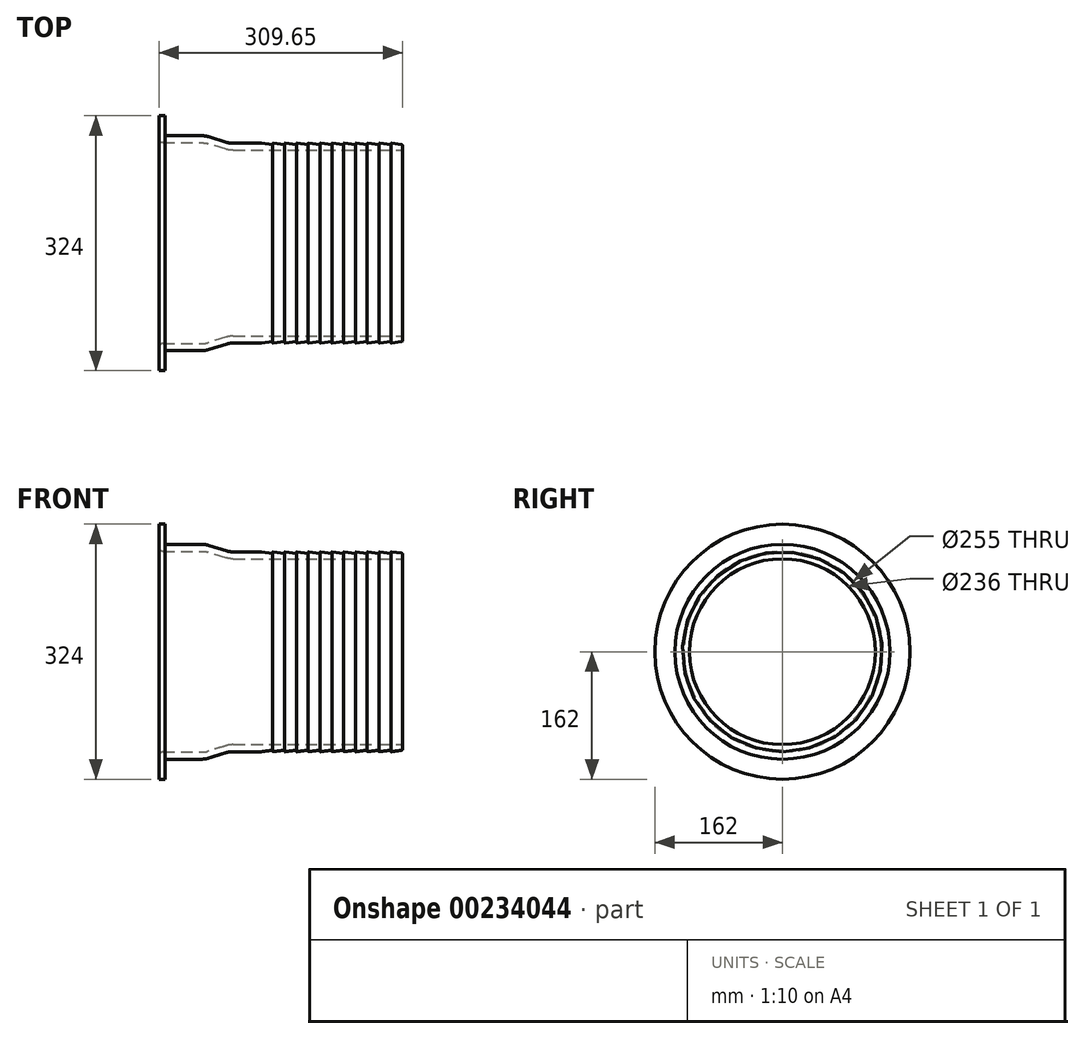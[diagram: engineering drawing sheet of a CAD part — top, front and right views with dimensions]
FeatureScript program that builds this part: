
annotation { "Feature Type Name" : "Feature", "Feature Type Description" : "" }
export const myFeature = defineFeature(function(context is Context, id is Id, definition is map)
    precondition{}
    {
        {
            var Q0;
            Q0=qCreatedBy(makeId("Front.planeOp"),FACE);
            var sketch = newSketch(context, id + "F0", { "sketchPlane" : qUnion([Q0])});
            skLineSegment(sketch, "E0", {"start": v(-1.73, 125.24) * mm, "end": v(-14.43, 127) * mm});
            skLineSegment(sketch, "E1", {"start": v(-15, 126.5) * mm, "end": v(-15, 125) * mm});
            skPoint(sketch, "E2.visualSharp", {"position": v(-15, 127.07) * mm});
            skArc(sketch, "E2.filletArc", {"start": v(-14.43, 127) * mm, "mid": v(-14.83, 126.88) * mm, "end": v(-15, 126.5) * mm});
            skLineSegment(sketch, "E3", {"start": v(0, 125) * mm, "end": v(-18.24, 125) * mm, "construction": true});
            skLineSegment(sketch, "E4", {"start": v(-7.53, 127) * mm, "end": v(-18.06, 127) * mm, "construction": true});
            skPoint(sketch, "E5", {"position": v(-14.5, 127) * mm});
            skLineSegment(sketch, "E6.1.0.0", {"start": v(-30, 126.5) * mm, "end": v(-30, 125) * mm});
            skArc(sketch, "E6.1.0.1", {"start": v(-29.43, 127) * mm, "mid": v(-29.83, 126.88) * mm, "end": v(-30, 126.5) * mm});
            skLineSegment(sketch, "E6.1.0.2", {"start": v(-15, 125) * mm, "end": v(-29.43, 127) * mm});
            skLineSegment(sketch, "E6.2.0.0", {"start": v(-45, 126.5) * mm, "end": v(-45, 125) * mm});
            skArc(sketch, "E6.2.0.1", {"start": v(-44.43, 127) * mm, "mid": v(-44.83, 126.88) * mm, "end": v(-45, 126.5) * mm});
            skLineSegment(sketch, "E6.2.0.2", {"start": v(-30, 125) * mm, "end": v(-44.43, 127) * mm});
            skLineSegment(sketch, "E6.3.0.0", {"start": v(-60, 126.5) * mm, "end": v(-60, 125) * mm});
            skArc(sketch, "E6.3.0.1", {"start": v(-59.43, 127) * mm, "mid": v(-59.83, 126.88) * mm, "end": v(-60, 126.5) * mm});
            skLineSegment(sketch, "E6.3.0.2", {"start": v(-45, 125) * mm, "end": v(-59.43, 127) * mm});
            skLineSegment(sketch, "E6.4.0.0", {"start": v(-75, 126.5) * mm, "end": v(-75, 125) * mm});
            skArc(sketch, "E6.4.0.1", {"start": v(-74.43, 127) * mm, "mid": v(-74.83, 126.88) * mm, "end": v(-75, 126.5) * mm});
            skLineSegment(sketch, "E6.4.0.2", {"start": v(-60, 125) * mm, "end": v(-74.43, 127) * mm});
            skLineSegment(sketch, "E6.5.0.0", {"start": v(-90, 126.5) * mm, "end": v(-90, 125) * mm});
            skArc(sketch, "E6.5.0.1", {"start": v(-89.43, 127) * mm, "mid": v(-89.83, 126.88) * mm, "end": v(-90, 126.5) * mm});
            skLineSegment(sketch, "E6.5.0.2", {"start": v(-75, 125) * mm, "end": v(-89.43, 127) * mm});
            skLineSegment(sketch, "E6.6.0.0", {"start": v(-105, 126.5) * mm, "end": v(-105, 125) * mm});
            skArc(sketch, "E6.6.0.1", {"start": v(-104.43, 127) * mm, "mid": v(-104.83, 126.88) * mm, "end": v(-105, 126.5) * mm});
            skLineSegment(sketch, "E6.6.0.2", {"start": v(-90, 125) * mm, "end": v(-104.43, 127) * mm});
            skLineSegment(sketch, "E6.7.0.0", {"start": v(-120, 126.5) * mm, "end": v(-120, 125) * mm});
            skArc(sketch, "E6.7.0.1", {"start": v(-119.43, 127) * mm, "mid": v(-119.83, 126.88) * mm, "end": v(-120, 126.5) * mm});
            skLineSegment(sketch, "E6.7.0.2", {"start": v(-105, 125) * mm, "end": v(-119.43, 127) * mm});
            skLineSegment(sketch, "E6.8.0.0", {"start": v(-135, 126.5) * mm, "end": v(-135, 125) * mm});
            skArc(sketch, "E6.8.0.1", {"start": v(-134.43, 127) * mm, "mid": v(-134.83, 126.88) * mm, "end": v(-135, 126.5) * mm});
            skLineSegment(sketch, "E6.8.0.2", {"start": v(-120, 125) * mm, "end": v(-134.43, 127) * mm});
            skLineSegment(sketch, "E6.9.0.0", {"start": v(-150, 126.5) * mm, "end": v(-150, 125) * mm});
            skArc(sketch, "E6.9.0.1", {"start": v(-149.43, 127) * mm, "mid": v(-149.83, 126.88) * mm, "end": v(-150, 126.5) * mm});
            skLineSegment(sketch, "E6.9.0.2", {"start": v(-135, 125) * mm, "end": v(-149.43, 127) * mm});
            skLineSegment(sketch, "E6.10.0.0", {"start": v(-165, 126.5) * mm, "end": v(-165, 125) * mm});
            skArc(sketch, "E6.10.0.1", {"start": v(-164.43, 127) * mm, "mid": v(-164.83, 126.88) * mm, "end": v(-165, 126.5) * mm});
            skLineSegment(sketch, "E6.10.0.2", {"start": v(-150, 125) * mm, "end": v(-164.43, 127) * mm});
            skLineSegment(sketch, "E6.11.0.0", {"start": v(-180, 126.5) * mm, "end": v(-180, 125) * mm});
            skArc(sketch, "E6.11.0.1", {"start": v(-179.43, 127) * mm, "mid": v(-179.83, 126.88) * mm, "end": v(-180, 126.5) * mm});
            skLineSegment(sketch, "E6.11.0.2", {"start": v(-165, 125) * mm, "end": v(-179.43, 127) * mm});
            skLineSegment(sketch, "E6.direction1", {"start": v(-15, 125) * mm, "end": v(-30, 125) * mm, "construction": true});
            skLineSegment(sketch, "E7", {"start": v(-179.5, 127) * mm, "end": v(-216.98, 127) * mm});
            skLineSegment(sketch, "E8", {"start": v(0, 123.26) * mm, "end": v(0, 120) * mm});
            skLineSegment(sketch, "E9", {"start": v(-2, 118) * mm, "end": v(-215.47, 118) * mm});
            skLineSegment(sketch, "E10", {"start": v(-222.88, 127.9) * mm, "end": v(-246.42, 135.16) * mm});
            skLineSegment(sketch, "E11", {"start": v(-255.27, 136.5) * mm, "end": v(-299.65, 136.5) * mm});
            skLineSegment(sketch, "E12", {"start": v(-301.65, 138.5) * mm, "end": v(-301.65, 162) * mm});
            skLineSegment(sketch, "E13", {"start": v(-301.65, 162) * mm, "end": v(-309.65, 162) * mm});
            skLineSegment(sketch, "E14", {"start": v(-309.65, 162) * mm, "end": v(-309.65, 132.5) * mm});
            skLineSegment(sketch, "E15", {"start": v(-224.33, 119.34) * mm, "end": v(-247.86, 126.6) * mm});
            skLineSegment(sketch, "E16", {"start": v(-253.76, 127.5) * mm, "end": v(-304.65, 127.5) * mm});
            skPoint(sketch, "E17.visualSharp", {"position": v(-250.74, 136.5) * mm});
            skArc(sketch, "E17.filletArc", {"start": v(-246.42, 135.16) * mm, "mid": v(-250.8, 136.16) * mm, "end": v(-255.27, 136.5) * mm});
            skPoint(sketch, "E18.visualSharp", {"position": v(-250.74, 127.5) * mm});
            skArc(sketch, "E18.filletArc", {"start": v(-247.86, 126.6) * mm, "mid": v(-250.78, 127.28) * mm, "end": v(-253.76, 127.5) * mm});
            skArc(sketch, "E19.filletArc", {"start": v(-222.88, 127.9) * mm, "mid": v(-219.97, 127.22) * mm, "end": v(-216.98, 127) * mm});
            skPoint(sketch, "E20.visualSharp", {"position": v(-220, 118) * mm});
            skArc(sketch, "E20.filletArc", {"start": v(-224.33, 119.34) * mm, "mid": v(-219.95, 118.34) * mm, "end": v(-215.47, 118) * mm});
            skPoint(sketch, "E21.visualSharp", {"position": v(-301.65, 136.5) * mm});
            skArc(sketch, "E21.filletArc", {"start": v(-301.65, 138.5) * mm, "mid": v(-301.07, 137.09) * mm, "end": v(-299.65, 136.5) * mm});
            skPoint(sketch, "E22.newPointA", {"position": v(-309.65, 118) * mm});
            skPoint(sketch, "E22.newPointB", {"position": v(-309.65, 127.5) * mm});
            skArc(sketch, "E22.filletArc", {"start": v(-309.65, 132.5) * mm, "mid": v(-308.2, 128.96) * mm, "end": v(-304.65, 127.5) * mm});
            skPoint(sketch, "E23.visualSharp", {"position": v(0, 125) * mm});
            skArc(sketch, "E23.filletArc", {"start": v(0, 123.26) * mm, "mid": v(-0.5, 124.57) * mm, "end": v(-1.73, 125.24) * mm});
            skPoint(sketch, "E24.visualSharp", {"position": v(0, 118) * mm});
            skArc(sketch, "E24.filletArc", {"start": v(-2, 118) * mm, "mid": v(-0.59, 118.59) * mm, "end": v(0, 120) * mm});
            skSolve(sketch);
        }
        {
            var Q0;
            Q0=qCreatedBy(makeId("Front.planeOp"),FACE);
            var sketch = newSketch(context, id + "F1", { "sketchPlane" : qUnion([Q0])});
            skLineSegment(sketch, "E25", {"start": v(45.17, 0) * mm, "end": v(-335.63, 0) * mm, "construction": true});
            skSolve(sketch);
        }
        {
            var Q0;
            Q0=makeQuery(id+"F0.imprint","IMPRINT",FACE,{"disambiguationData":[TD([[makeQuery(id+"F0.imprint","IMPRINT",EDGE,{"derivedFrom":sQuery(id+"F0.wireOp",EDGE,"E0")}),1.0]])]});
            var Q1;
            Q1=sQuery(id+"F1.wireOp",EDGE,"E25");
            revolve(context, id + "F2", {"entities" : qUnion([Q0]), "axis" : qUnion([Q1]), "revolveType" : RevolveType.FULL});
        }
    });
